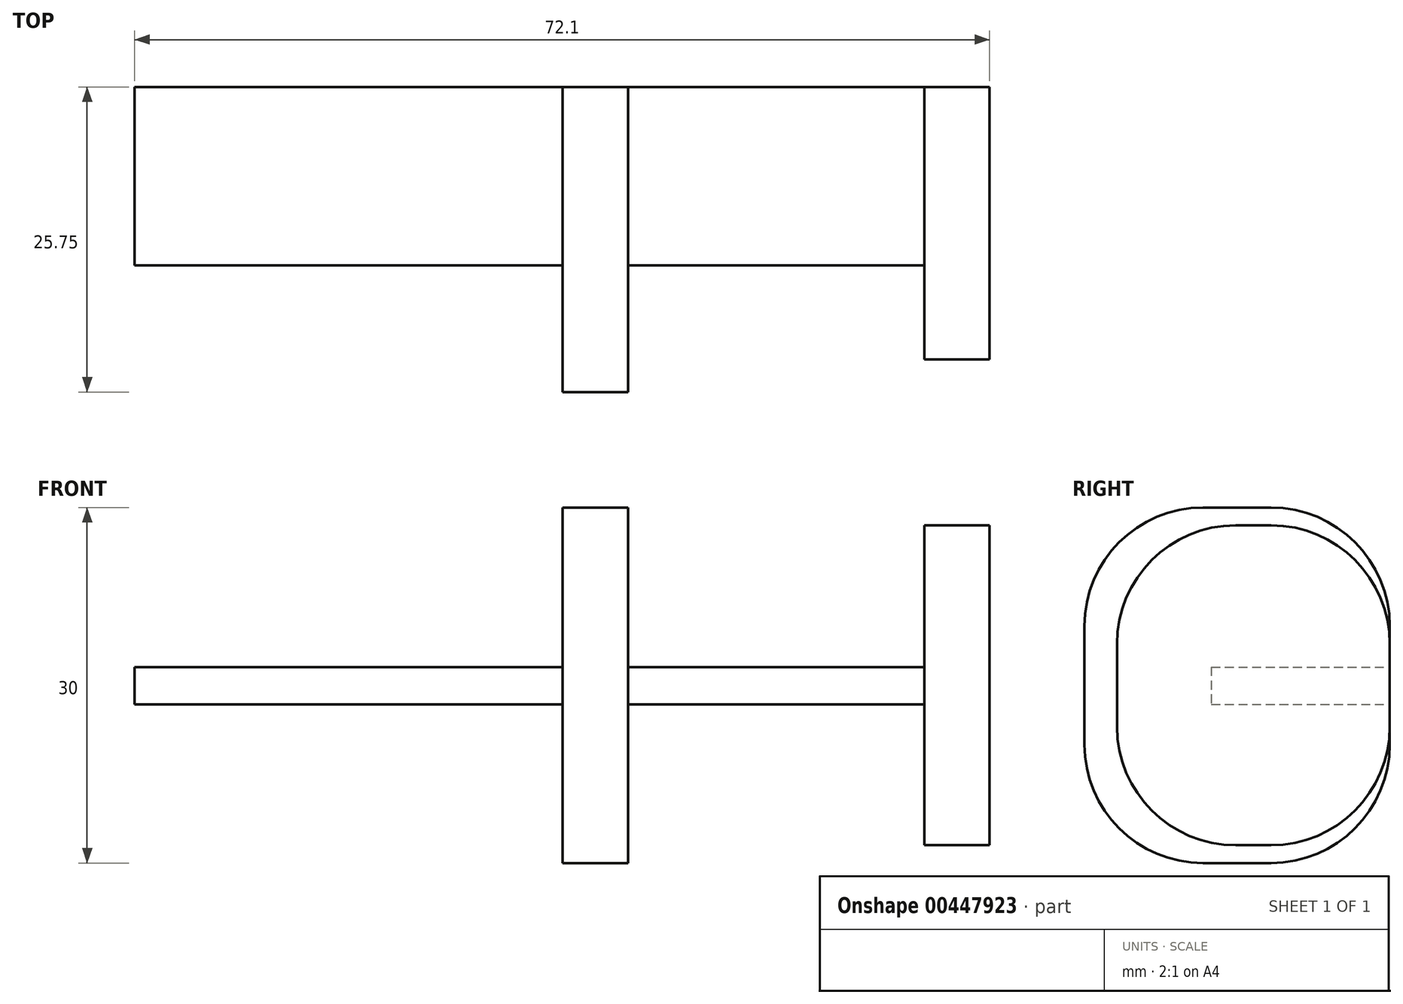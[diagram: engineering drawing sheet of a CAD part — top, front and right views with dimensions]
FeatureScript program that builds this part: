
annotation { "Feature Type Name" : "Feature", "Feature Type Description" : "" }
export const myFeature = defineFeature(function(context is Context, id is Id, definition is map)
    precondition{}
    {
        {
            var Q0;
            Q0=qCreatedBy(makeId("Front.planeOp"),FACE);
            var sketch = newSketch(context, id + "F0", { "sketchPlane" : qUnion([Q0])});
            skLineSegment(sketch, "E0.bottom", {"start": v(2.75, -13.5) * mm, "end": v(-2.75, -13.5) * mm});
            skLineSegment(sketch, "E0.top", {"start": v(2.75, 13.5) * mm, "end": v(-2.75, 13.5) * mm});
            skLineSegment(sketch, "E0.left", {"start": v(2.75, -13.5) * mm, "end": v(2.75, 13.5) * mm});
            skLineSegment(sketch, "E0.right", {"start": v(-2.75, -13.5) * mm, "end": v(-2.75, 13.5) * mm});
            skPoint(sketch, "E0.middle", {"position": v(0, 0) * mm});
            skLineSegment(sketch, "E1.bottom", {"start": v(-27.75, -15) * mm, "end": v(-33.25, -15) * mm});
            skLineSegment(sketch, "E1.top", {"start": v(-27.75, 15) * mm, "end": v(-33.25, 15) * mm});
            skLineSegment(sketch, "E1.left", {"start": v(-27.75, -15) * mm, "end": v(-27.75, 15) * mm});
            skLineSegment(sketch, "E1.right", {"start": v(-33.25, -15) * mm, "end": v(-33.25, 15) * mm});
            skPoint(sketch, "E1.middle", {"position": v(-30.5, 0) * mm});
            skSolve(sketch);
        }
        {
            var Q0;
            Q0 = qSketchRegion(id + "F0", true);
            extrude(context, id + "F1", {"entities" : qUnion([Q0]), "depth" : 23 * mm});
        }
        {
            var Q0;
            Q0=makeQuery(id+"F1.opExtrude","CAP_FACE",FACE,{"disambiguationData":[OSD([sQuery(id+"F0.wireOp",EDGE,"E1.bottom"),sQuery(id+"F0.wireOp",EDGE,"E1.top"),sQuery(id+"F0.wireOp",EDGE,"E1.left"),sQuery(id+"F0.wireOp",EDGE,"E1.right")])],"isStart":false});
            extrude(context, id + "F2", {"entities" : qUnion([Q0]), "operationType" : NewBodyOperationType.ADD, "endBound" : BoundingType.SYMMETRIC, "depth" : 5.5 * mm});
        }
        {
            var Q0;
            Q0=makeQuery(id+"F1.opExtrude","CAP_EDGE",EDGE,{"disambiguationData":[OSD([sQuery(id+"F0.wireOp",EDGE,"E0.bottom")])],"isStart":false});
            var Q1;
            Q1=makeQuery(id+"F1.opExtrude","CAP_EDGE",EDGE,{"disambiguationData":[OSD([sQuery(id+"F0.wireOp",EDGE,"E0.top")])],"isStart":false});
            var Q2;
            Q2=makeQuery(id+"F1.opExtrude","CAP_EDGE",EDGE,{"disambiguationData":[OSD([sQuery(id+"F0.wireOp",EDGE,"E0.bottom")])],"isStart":true});
            var Q3;
            Q3=makeQuery(id+"F1.opExtrude","CAP_EDGE",EDGE,{"disambiguationData":[OSD([sQuery(id+"F0.wireOp",EDGE,"E0.top")])],"isStart":true});
            fillet(context, id + "F3", {"entities" : qUnion([Q0, Q1, Q2, Q3]), "radius" : 10 * mm, "tangentPropagation" : true, "allowEdgeOverflow" : false});
        }
        {
            var Q0;
            Q0=makeQuery(id+"F1.opExtrude","CAP_EDGE",EDGE,{"disambiguationData":[OSD([sQuery(id+"F0.wireOp",EDGE,"E1.top")])],"isStart":true});
            var Q1;
            Q1=makeQuery(id+"F1.opExtrude","CAP_EDGE",EDGE,{"disambiguationData":[OSD([sQuery(id+"F0.wireOp",EDGE,"E1.bottom")])],"isStart":true});
            var Q2;
            Q2=makeQuery(id+"F2.opExtrude","CAP_EDGE",EDGE,{"disambiguationData":[OSD([sQuery(id+"F0.wireOp",EDGE,"E1.bottom")])],"isStart":false});
            var Q3;
            Q3=makeQuery(id+"F2.opExtrude","CAP_EDGE",EDGE,{"disambiguationData":[OSD([sQuery(id+"F0.wireOp",EDGE,"E1.top")])],"isStart":false});
            fillet(context, id + "F4", {"entities" : qUnion([Q0, Q1, Q2, Q3]), "radius" : 10 * mm, "tangentPropagation" : true, "allowEdgeOverflow" : false});
        }
        {
            var Q0;
            Q0=makeQuery(id+"F1.opExtrude","SWEPT_FACE",FACE,{"disambiguationData":[OSD([sQuery(id+"F0.wireOp",EDGE,"E0.left")])]});
            var sketch = newSketch(context, id + "F5", { "sketchPlane" : qUnion([Q0])});
            skLineSegment(sketch, "E2.bottom", {"start": v(0, -1.6) * mm, "end": v(-15.05, -1.6) * mm});
            skLineSegment(sketch, "E2.top", {"start": v(0, 1.54) * mm, "end": v(-15.05, 1.54) * mm});
            skLineSegment(sketch, "E2.left", {"start": v(0, -1.6) * mm, "end": v(0, 1.54) * mm});
            skLineSegment(sketch, "E2.right", {"start": v(-15.05, -1.6) * mm, "end": v(-15.05, 1.54) * mm});
            skSolve(sketch);
        }
        {
            var Q0;
            Q0=makeQuery(id+"F5.imprint","IMPRINT",FACE,{"disambiguationData":[TD([[makeQuery(id+"F5.imprint","IMPRINT",EDGE,{"derivedFrom":sQuery(id+"F5.wireOp",EDGE,"E2.bottom")}),-1.0]])]});
            extrude(context, id + "F6", {"entities" : qUnion([Q0]), "operationType" : NewBodyOperationType.ADD, "oppositeDirection" : true, "depth" : 72.1 * mm});
        }
    });
